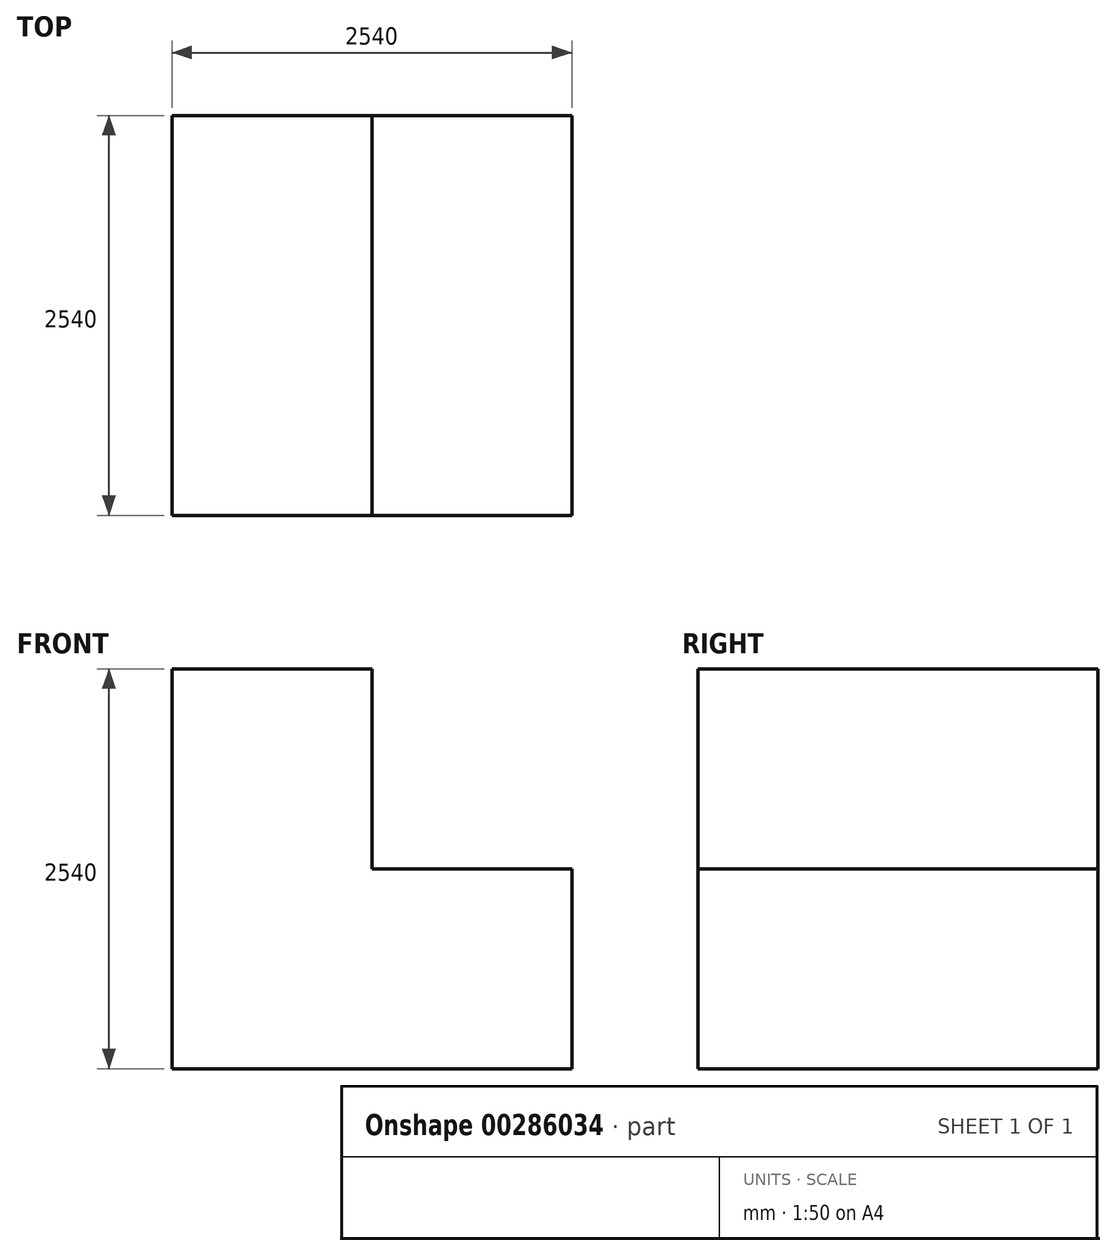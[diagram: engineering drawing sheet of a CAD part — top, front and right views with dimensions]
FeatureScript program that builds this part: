
annotation { "Feature Type Name" : "Feature", "Feature Type Description" : "" }
export const myFeature = defineFeature(function(context is Context, id is Id, definition is map)
    precondition{}
    {
        {
            var Q0;
            Q0=qCreatedBy(makeId("Front.planeOp"),FACE);
            var sketch = newSketch(context, id + "F0", { "sketchPlane" : qUnion([Q0])});
            skLineSegment(sketch, "E0", {"start": v(-1604.84, 2184.79) * mm, "end": v(-1604.84, -355.21) * mm});
            skLineSegment(sketch, "E1", {"start": v(-1604.84, -355.21) * mm, "end": v(935.16, -355.21) * mm});
            skLineSegment(sketch, "E2", {"start": v(935.16, -355.21) * mm, "end": v(935.16, 914.79) * mm});
            skLineSegment(sketch, "E3", {"start": v(935.16, 914.79) * mm, "end": v(-334.84, 914.79) * mm});
            skLineSegment(sketch, "E4", {"start": v(-334.84, 914.79) * mm, "end": v(-334.84, 2184.79) * mm});
            skLineSegment(sketch, "E5", {"start": v(-334.84, 2184.79) * mm, "end": v(-1604.84, 2184.79) * mm});
            skSolve(sketch);
        }
        {
            var Q0;
            Q0 = qSketchRegion(id + "F0", true);
            extrude(context, id + "F1", {"entities" : qUnion([Q0]), "depth" : 2540 * mm});
        }
    });
